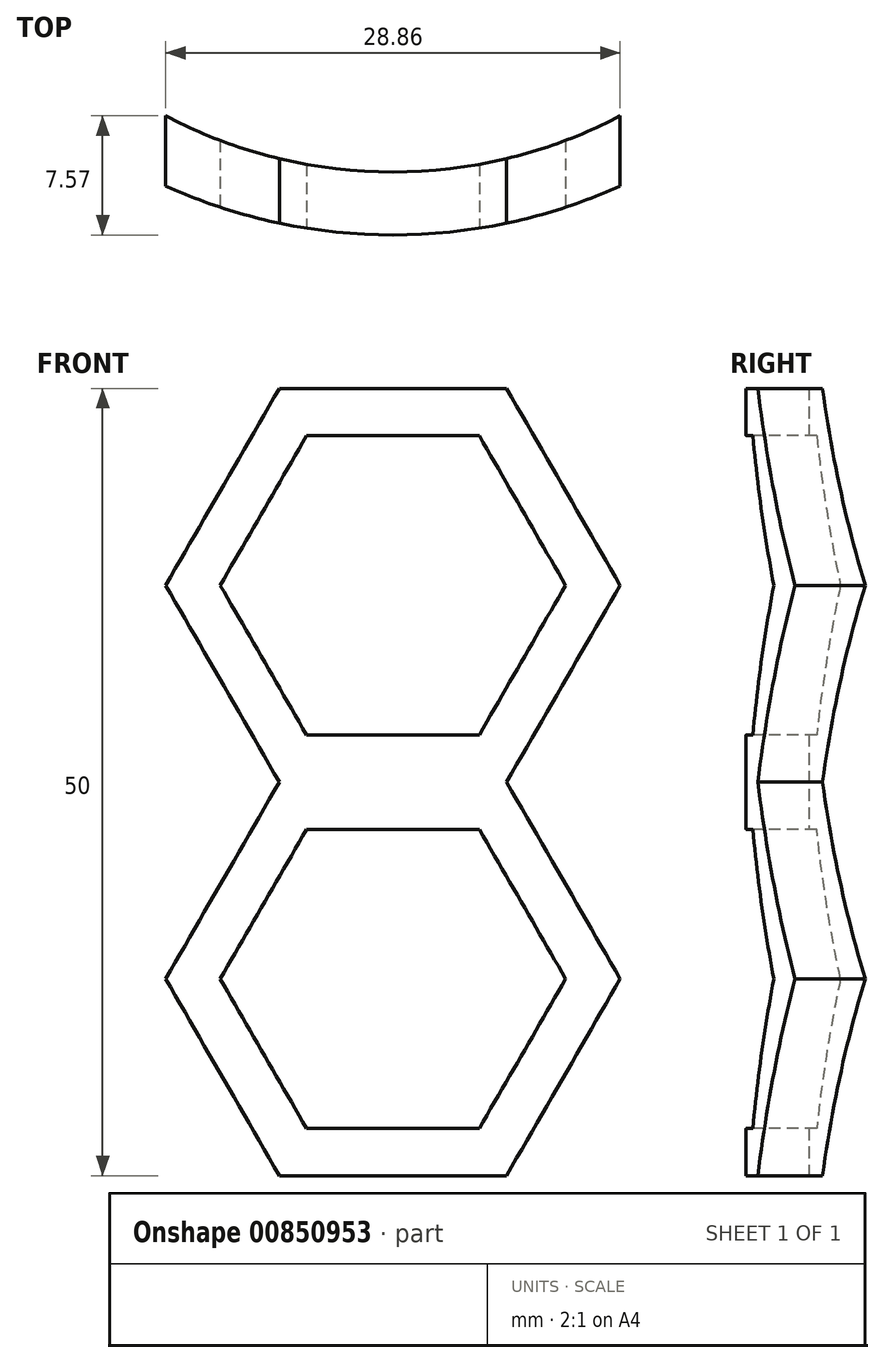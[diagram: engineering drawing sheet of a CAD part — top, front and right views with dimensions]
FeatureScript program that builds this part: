
annotation { "Feature Type Name" : "Feature", "Feature Type Description" : "" }
export const myFeature = defineFeature(function(context is Context, id is Id, definition is map)
    precondition{}
    {
        {
            var Q0;
            Q0=qCreatedBy(makeId("Top.planeOp"),FACE);
            var sketch = newSketch(context, id + "F0", { "sketchPlane" : qUnion([Q0])});
            skCircle(sketch, "E0", {"center": v(0, 0) * mm, "radius": 31 * mm});
            skCircle(sketch, "E1", {"center": v(0, 0) * mm, "radius": 35 * mm});
            skSolve(sketch);
        }
        {
            var Q0;
            Q0=makeQuery(id+"F0.imprint","IMPRINT",FACE,{"disambiguationData":[TD([[makeQuery(id+"F0.imprint","IMPRINT",EDGE,{"derivedFrom":sQuery(id+"F0.wireOp",EDGE,"E0")}),-1.0]])]});
            extrude(context, id + "F1", {"entities" : qUnion([Q0]), "depth" : 50 * mm, "offsetDistance" : 25 * mm});
        }
        {
            var Q0;
            Q0=qCreatedBy(makeId("Front.planeOp"),FACE);
            cPlane(context, id + "F2", {"entities" : qUnion([Q0]), "cplaneType" : CPlaneType.OFFSET, "offset" : 60 * mm, "width" : 150 * mm, "height" : 150 * mm});
        }
        {
            var Q0;
            Q0=qCreatedBy(id+"F2.planeOp",FACE);
            var sketch = newSketch(context, id + "F3", { "sketchPlane" : qUnion([Q0])});
            skCircle(sketch, "E2.cCircle", {"center": v(0, 12.5) * mm, "radius": 12.5 * mm, "construction": true});
            skLineSegment(sketch, "E2.0", {"start": v(14.43, 12.5) * mm, "end": v(7.22, 0) * mm});
            skLineSegment(sketch, "E2.1", {"start": v(7.22, 0) * mm, "end": v(-7.22, 0) * mm});
            skLineSegment(sketch, "E2.2", {"start": v(-7.22, 0) * mm, "end": v(-14.43, 12.5) * mm});
            skLineSegment(sketch, "E2.3", {"start": v(-14.43, 12.5) * mm, "end": v(-7.22, 25) * mm});
            skLineSegment(sketch, "E2.4", {"start": v(-7.22, 25) * mm, "end": v(7.22, 25) * mm});
            skLineSegment(sketch, "E2.5", {"start": v(7.22, 25) * mm, "end": v(14.43, 12.5) * mm});
            skPoint(sketch, "E2.0.midPoint", {"position": v(10.83, 6.25) * mm});
            skCircle(sketch, "E3.cCircle", {"center": v(0, 12.5) * mm, "radius": 9.5 * mm, "construction": true});
            skLineSegment(sketch, "E3.0", {"start": v(5.48, 3) * mm, "end": v(-5.48, 3) * mm});
            skLineSegment(sketch, "E3.1", {"start": v(-5.48, 3) * mm, "end": v(-10.97, 12.5) * mm});
            skLineSegment(sketch, "E3.2", {"start": v(-10.97, 12.5) * mm, "end": v(-5.48, 22) * mm});
            skLineSegment(sketch, "E3.3", {"start": v(-5.48, 22) * mm, "end": v(5.48, 22) * mm});
            skLineSegment(sketch, "E3.4", {"start": v(5.48, 22) * mm, "end": v(10.97, 12.5) * mm});
            skLineSegment(sketch, "E3.5", {"start": v(10.97, 12.5) * mm, "end": v(5.48, 3) * mm});
            skPoint(sketch, "E3.0.midPoint", {"position": v(0, 3) * mm});
            skCircle(sketch, "E4.cCircle", {"center": v(0, 37.5) * mm, "radius": 12.5 * mm, "construction": true});
            skLineSegment(sketch, "E4.0", {"start": v(14.43, 37.5) * mm, "end": v(7.22, 25) * mm});
            skLineSegment(sketch, "E4.1", {"start": v(7.22, 25) * mm, "end": v(-7.22, 25) * mm});
            skLineSegment(sketch, "E4.2", {"start": v(-7.22, 25) * mm, "end": v(-14.43, 37.5) * mm});
            skLineSegment(sketch, "E4.3", {"start": v(-14.43, 37.5) * mm, "end": v(-7.22, 50) * mm});
            skLineSegment(sketch, "E4.4", {"start": v(-7.22, 50) * mm, "end": v(7.22, 50) * mm});
            skLineSegment(sketch, "E4.5", {"start": v(7.22, 50) * mm, "end": v(14.43, 37.5) * mm});
            skPoint(sketch, "E4.0.midPoint", {"position": v(10.83, 31.25) * mm});
            skCircle(sketch, "E5.cCircle", {"center": v(0, 37.5) * mm, "radius": 9.5 * mm, "construction": true});
            skLineSegment(sketch, "E5.0", {"start": v(10.97, 37.5) * mm, "end": v(5.48, 28) * mm});
            skLineSegment(sketch, "E5.1", {"start": v(5.48, 28) * mm, "end": v(-5.48, 28) * mm});
            skLineSegment(sketch, "E5.2", {"start": v(-5.48, 28) * mm, "end": v(-10.97, 37.5) * mm});
            skLineSegment(sketch, "E5.3", {"start": v(-10.97, 37.5) * mm, "end": v(-5.48, 47) * mm});
            skLineSegment(sketch, "E5.4", {"start": v(-5.48, 47) * mm, "end": v(5.48, 47) * mm});
            skLineSegment(sketch, "E5.5", {"start": v(5.48, 47) * mm, "end": v(10.97, 37.5) * mm});
            skPoint(sketch, "E5.0.midPoint", {"position": v(8.23, 32.75) * mm});
            skSolve(sketch);
        }
        {
            var Q0;
            Q0=makeQuery(id+"F3.imprint","IMPRINT",FACE,{"disambiguationData":[TD([[makeQuery(id+"F3.imprint","IMPRINT",EDGE,{"derivedFrom":sQuery(id+"F3.wireOp",EDGE,"E4.0")}),-1.0]])]});
            var Q1;
            Q1=makeQuery(id+"F3.imprint","IMPRINT",FACE,{"disambiguationData":[TD([[makeQuery(id+"F3.imprint","IMPRINT",EDGE,{"derivedFrom":sQuery(id+"F3.wireOp",EDGE,"E2.0")}),-1.0]])]});
            extrude(context, id + "F4", {"entities" : qUnion([Q0, Q1]), "operationType" : NewBodyOperationType.INTERSECT, "oppositeDirection" : true, "depth" : 50 * mm, "offsetDistance" : 25 * mm});
        }
    });
